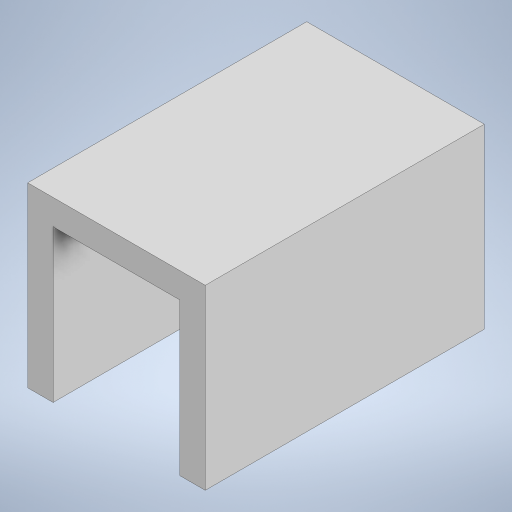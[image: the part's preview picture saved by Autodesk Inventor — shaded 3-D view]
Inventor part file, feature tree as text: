
AUTODESK INVENTOR PART (.ipt)
format: ipt  version: 2023 (Build 270158000, 158)  size: 180,736 bytes
history: native  units: in
note: dims shown in document units (in); Inventor stores cm internally (conversion verified against a paired STEP export)
features: extrude x3, sketch x3
ambient origin geometry x8: Origin, YZ Plane, XZ Plane, XY Plane, X Axis, Y Axis, Z Axis, Center Point
bodies: Solid1 (feature_tree)
feature tree (6):
  extrude  "Extrusion1"  Depth=0.5512in
  extrude  "Extrusion2"  Depth=0.3937in
  extrude  "Extrusion3"  Depth=0.7874in TaperAngle=0.0deg
  sketch  "Sketch1"  dims[d0=0.5512in d1=0.5512in]
  sketch  "Sketch2"  dims[d2=0.8661in d3=0.0in d4=0.3937in]
  sketch  "Sketch3"  dims[d5=0.7874in d6=0.7874in d7=0.0in d8=0.1181in d9=0.3937in d10=0.0in]
